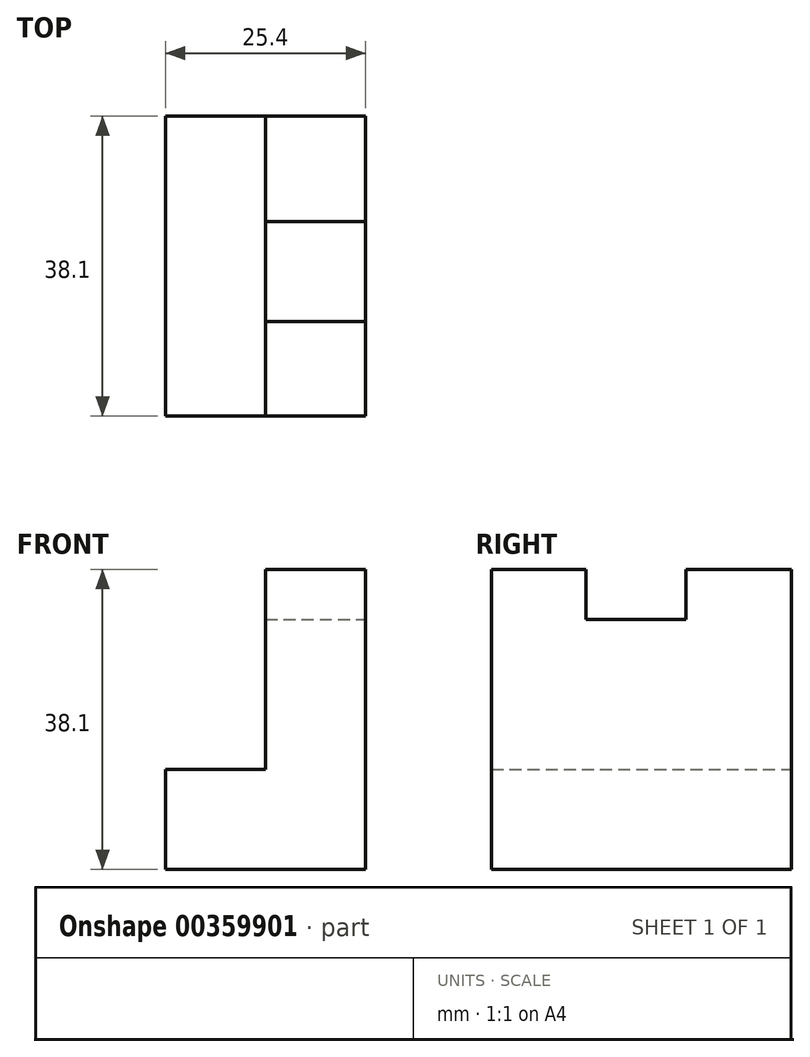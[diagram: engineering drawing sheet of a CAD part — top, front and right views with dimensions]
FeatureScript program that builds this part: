
annotation { "Feature Type Name" : "Feature", "Feature Type Description" : "" }
export const myFeature = defineFeature(function(context is Context, id is Id, definition is map)
    precondition{}
    {
        {
            var Q0;
            Q0=qCreatedBy(makeId("Front.planeOp"),FACE);
            var sketch = newSketch(context, id + "F0", { "sketchPlane" : qUnion([Q0])});
            skLineSegment(sketch, "E0", {"start": v(0, 0) * mm, "end": v(0, 12.7) * mm});
            skLineSegment(sketch, "E1", {"start": v(0, 12.7) * mm, "end": v(12.7, 12.7) * mm});
            skLineSegment(sketch, "E2", {"start": v(12.7, 12.7) * mm, "end": v(12.7, 31.75) * mm});
            skLineSegment(sketch, "E3", {"start": v(12.7, 31.75) * mm, "end": v(25.4, 31.75) * mm});
            skLineSegment(sketch, "E4", {"start": v(25.4, 31.75) * mm, "end": v(25.4, 0) * mm});
            skLineSegment(sketch, "E5", {"start": v(25.4, 0) * mm, "end": v(0, 0) * mm});
            skSolve(sketch);
        }
        {
            var Q0;
            Q0 = qSketchRegion(id + "F0", true);
            extrude(context, id + "F1", {"entities" : qUnion([Q0]), "depth" : 38.1 * mm});
        }
        {
            var Q0;
            Q0=makeQuery(id+"F1.opExtrude","SWEPT_FACE",FACE,{"disambiguationData":[OSD([sQuery(id+"F0.wireOp",EDGE,"E3")])]});
            var sketch = newSketch(context, id + "F2", { "sketchPlane" : qUnion([Q0])});
            skLineSegment(sketch, "E6", {"start": v(12.7, 0) * mm, "end": v(12.7, -38.1) * mm});
            skLineSegment(sketch, "E7", {"start": v(12.7, -38.1) * mm, "end": v(25.4, -38.1) * mm});
            skLineSegment(sketch, "E8", {"start": v(25.4, -38.1) * mm, "end": v(25.4, 0) * mm});
            skLineSegment(sketch, "E9", {"start": v(25.4, 0) * mm, "end": v(12.7, 0) * mm});
            skLineSegment(sketch, "E10", {"start": v(12.7, -13.4) * mm, "end": v(25.4, -13.4) * mm});
            skLineSegment(sketch, "E11", {"start": v(25.4, -13.4) * mm, "end": v(25.4, -26.1) * mm});
            skLineSegment(sketch, "E12", {"start": v(25.4, -26.1) * mm, "end": v(12.7, -26.1) * mm});
            skLineSegment(sketch, "E13", {"start": v(12.7, -26.1) * mm, "end": v(12.7, -13.4) * mm});
            skSolve(sketch);
        }
        {
            var Q0;
            {var subQ0=sQuery(id+"F2.wireOp",EDGE,"E7");Q0=makeQuery(id+"F2.imprint","IMPRINT",FACE,{"disambiguationData":[TD([[makeQuery(id+"F2.imprint","IMPRINT",EDGE,{"derivedFrom":subQ0}),1.0]])]});}
            var Q1;
            {var subQ0=sQuery(id+"F2.wireOp",EDGE,"E9");Q1=makeQuery(id+"F2.imprint","IMPRINT",FACE,{"disambiguationData":[TD([[makeQuery(id+"F2.imprint","IMPRINT",EDGE,{"derivedFrom":subQ0}),-1.0]])]});}
            extrude(context, id + "F3", {"entities" : qUnion([Q0, Q1]), "operationType" : NewBodyOperationType.ADD, "depth" : 6.35 * mm});
        }
    });
